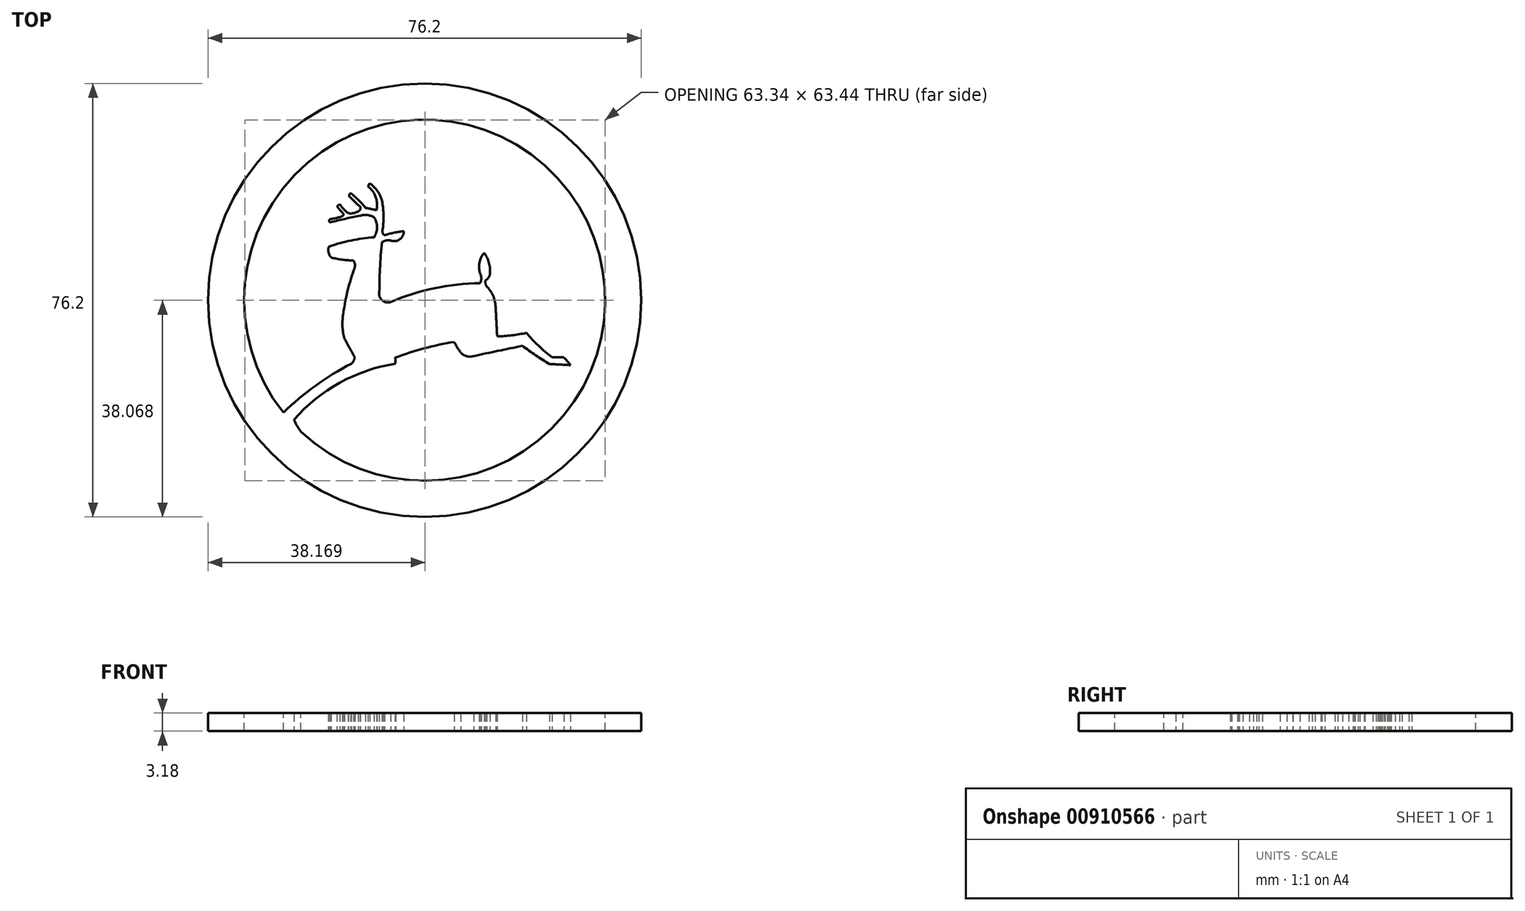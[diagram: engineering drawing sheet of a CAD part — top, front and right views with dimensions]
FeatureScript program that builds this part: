
annotation { "Feature Type Name" : "Feature", "Feature Type Description" : "" }
export const myFeature = defineFeature(function(context is Context, id is Id, definition is map)
    precondition{}
    {
        {
            var Q0;
            Q0=qCreatedBy(makeId("Top.planeOp"),FACE);
            var sketch = newSketch(context, id + "F0", { "sketchPlane" : qUnion([Q0])});
            skArc(sketch, "E0", {"start": v(40.39, 34.09) * mm, "mid": v(30.63, 30.74) * mm, "end": v(22.62, 24.25) * mm});
            skArc(sketch, "E1", {"start": v(50.78, 37.92) * mm, "mid": v(45.51, 36.8) * mm, "end": v(40.39, 35.14) * mm});
            skArc(sketch, "E2", {"start": v(40.39, 34.09) * mm, "mid": v(40.48, 34.61) * mm, "end": v(40.39, 35.14) * mm});
            skArc(sketch, "E3", {"start": v(50.78, 37.92) * mm, "mid": v(51.3, 36.98) * mm, "end": v(51.92, 36.1) * mm});
            skArc(sketch, "E4", {"start": v(51.92, 36.1) * mm, "mid": v(52.98, 35.4) * mm, "end": v(54.24, 35.43) * mm});
            skArc(sketch, "E5", {"start": v(62.79, 37.23) * mm, "mid": v(58.51, 36.35) * mm, "end": v(54.24, 35.43) * mm});
            skArc(sketch, "E6", {"start": v(62.79, 37.23) * mm, "mid": v(65.13, 35.57) * mm, "end": v(67.57, 34.04) * mm});
            skArc(sketch, "E7", {"start": v(71.27, 33.84) * mm, "mid": v(69.42, 33.94) * mm, "end": v(67.57, 34.04) * mm});
            skArc(sketch, "E8", {"start": v(71.27, 33.84) * mm, "mid": v(70.7, 34.53) * mm, "end": v(70.1, 35.2) * mm});
            skArc(sketch, "E9", {"start": v(63.47, 39.51) * mm, "mid": v(65.64, 37.24) * mm, "end": v(68.03, 35.2) * mm});
            skArc(sketch, "E10", {"start": v(58.35, 38.9) * mm, "mid": v(60.92, 39.08) * mm, "end": v(63.47, 39.51) * mm});
            skArc(sketch, "E11", {"start": v(58.35, 38.9) * mm, "mid": v(58.22, 41.35) * mm, "end": v(58.07, 43.8) * mm});
            skArc(sketch, "E12", {"start": v(58.07, 43.8) * mm, "mid": v(57.7, 45.9) * mm, "end": v(56.5, 47.67) * mm});
            skArc(sketch, "E13", {"start": v(57.07, 49.79) * mm, "mid": v(56.92, 51.78) * mm, "end": v(56.07, 53.6) * mm});
            skArc(sketch, "E14", {"start": v(56.07, 53.6) * mm, "mid": v(55.23, 51.88) * mm, "end": v(55.34, 49.97) * mm});
            skArc(sketch, "E15", {"start": v(55.34, 48.24) * mm, "mid": v(55.55, 49.1) * mm, "end": v(55.34, 49.97) * mm});
            skArc(sketch, "E16", {"start": v(56.3, 48.76) * mm, "mid": v(56.79, 49.2) * mm, "end": v(57.07, 49.79) * mm});
            skArc(sketch, "E17", {"start": v(56.3, 48.76) * mm, "mid": v(56.3, 48.2) * mm, "end": v(56.5, 47.67) * mm});
            skArc(sketch, "E18", {"start": v(55.34, 48.24) * mm, "mid": v(47.3, 47.38) * mm, "end": v(39.62, 44.91) * mm});
            skArc(sketch, "E19", {"start": v(37.6, 46.1) * mm, "mid": v(38.36, 45.07) * mm, "end": v(39.62, 44.91) * mm});
            skArc(sketch, "E20", {"start": v(38.07, 55.46) * mm, "mid": v(37.73, 50.79) * mm, "end": v(37.6, 46.1) * mm});
            skArc(sketch, "E21", {"start": v(39.62, 55.76) * mm, "mid": v(38.81, 55.75) * mm, "end": v(38.07, 55.46) * mm});
            skArc(sketch, "E22", {"start": v(39.62, 55.76) * mm, "mid": v(41.2, 55.96) * mm, "end": v(41.92, 57.4) * mm});
            skArc(sketch, "E23", {"start": v(41.92, 57.4) * mm, "mid": v(40.22, 57.13) * mm, "end": v(38.57, 56.67) * mm});
            skArc(sketch, "E24", {"start": v(36.68, 56.33) * mm, "mid": v(37.22, 58.07) * mm, "end": v(36.7, 59.81) * mm});
            skArc(sketch, "E25", {"start": v(36.7, 59.81) * mm, "mid": v(35.48, 60.24) * mm, "end": v(34.2, 60.09) * mm});
            skArc(sketch, "E26", {"start": v(34.2, 60.09) * mm, "mid": v(31.6, 59.57) * mm, "end": v(29.02, 58.95) * mm});
            skArc(sketch, "E27", {"start": v(29.02, 59.52) * mm, "mid": v(28.8, 59.23) * mm, "end": v(29.02, 58.95) * mm});
            skArc(sketch, "E28", {"start": v(29.02, 59.52) * mm, "mid": v(30.14, 59.73) * mm, "end": v(31.23, 60.09) * mm});
            skArc(sketch, "E29", {"start": v(31.23, 60.09) * mm, "mid": v(31.3, 60.34) * mm, "end": v(31.23, 60.59) * mm});
            skArc(sketch, "E30", {"start": v(30.18, 61.75) * mm, "mid": v(30.68, 61.15) * mm, "end": v(31.23, 60.59) * mm});
            skArc(sketch, "E31", {"start": v(37.13, 61.1) * mm, "mid": v(36.16, 61.3) * mm, "end": v(35.2, 61.5) * mm});
            skArc(sketch, "E32", {"start": v(33.87, 60.9) * mm, "mid": v(34.3, 61.41) * mm, "end": v(33.9, 61.96) * mm});
            skArc(sketch, "E33", {"start": v(32.12, 60.59) * mm, "mid": v(33.03, 60.55) * mm, "end": v(33.87, 60.9) * mm});
            skArc(sketch, "E34", {"start": v(38.18, 62.18) * mm, "mid": v(37.44, 64.22) * mm, "end": v(35.95, 65.81) * mm});
            skArc(sketch, "E35", {"start": v(37.11, 62.9) * mm, "mid": v(36.6, 64.22) * mm, "end": v(35.63, 65.25) * mm});
            skArc(sketch, "E36", {"start": v(37.13, 61.1) * mm, "mid": v(37.23, 62) * mm, "end": v(37.11, 62.9) * mm});
            skArc(sketch, "E37", {"start": v(35.2, 61.5) * mm, "mid": v(33.95, 62.87) * mm, "end": v(32.57, 64.1) * mm});
            skArc(sketch, "E38", {"start": v(33.9, 61.96) * mm, "mid": v(33.07, 62.81) * mm, "end": v(32.2, 63.63) * mm});
            skArc(sketch, "E39", {"start": v(38.18, 57.56) * mm, "mid": v(38.36, 59.87) * mm, "end": v(38.18, 62.18) * mm});
            skArc(sketch, "E40", {"start": v(38.18, 57.56) * mm, "mid": v(38.22, 57.05) * mm, "end": v(38.57, 56.67) * mm});
            skArc(sketch, "E41", {"start": v(30.64, 62.18) * mm, "mid": v(31.3, 61.32) * mm, "end": v(32.12, 60.59) * mm});
            skLineSegment(sketch, "E42", {"start": v(35.95, 65.81) * mm, "end": v(35.63, 65.25) * mm});
            skLineSegment(sketch, "E43", {"start": v(32.57, 64.1) * mm, "end": v(32.2, 63.63) * mm});
            skLineSegment(sketch, "E44", {"start": v(30.64, 62.18) * mm, "end": v(30.18, 61.75) * mm});
            skArc(sketch, "E45", {"start": v(36.68, 56.33) * mm, "mid": v(32.65, 55.75) * mm, "end": v(28.73, 54.69) * mm});
            skArc(sketch, "E46", {"start": v(28.73, 54.69) * mm, "mid": v(28.69, 53.68) * mm, "end": v(29.14, 52.77) * mm});
            skArc(sketch, "E47", {"start": v(29.14, 52.77) * mm, "mid": v(31.11, 52.39) * mm, "end": v(33.1, 52.25) * mm});
            skArc(sketch, "E48", {"start": v(33.1, 50.5) * mm, "mid": v(33.32, 51.37) * mm, "end": v(33.1, 52.25) * mm});
            skArc(sketch, "E49", {"start": v(33.1, 50.5) * mm, "mid": v(31.96, 46.61) * mm, "end": v(31.24, 42.63) * mm});
            skArc(sketch, "E50", {"start": v(31.24, 42.63) * mm, "mid": v(31.14, 40.54) * mm, "end": v(31.51, 38.49) * mm});
            skArc(sketch, "E51", {"start": v(31.51, 38.49) * mm, "mid": v(32.37, 36.88) * mm, "end": v(33.27, 35.3) * mm});
            skArc(sketch, "E52", {"start": v(32.68, 34.11) * mm, "mid": v(33.11, 34.63) * mm, "end": v(33.27, 35.3) * mm});
            skArc(sketch, "E53", {"start": v(32.68, 34.11) * mm, "mid": v(25.94, 29.89) * mm, "end": v(19.92, 24.7) * mm});
            skLineSegment(sketch, "E54", {"start": v(19.92, 24.7) * mm, "end": v(22.62, 24.25) * mm});
            skLineSegment(sketch, "E55", {"start": v(70.1, 35.2) * mm, "end": v(68.03, 35.2) * mm});
            skLineSegment(sketch, "E56", {"start": v(29.13, 16.25) * mm, "end": v(29.13, 22.07) * mm});
            skLineSegment(sketch, "E57", {"start": v(29.13, 22.07) * mm, "end": v(30.21, 22.07) * mm});
            skLineSegment(sketch, "E58", {"start": v(30.21, 22.07) * mm, "end": v(30.21, 19.61) * mm});
            skLineSegment(sketch, "E59", {"start": v(30.21, 19.61) * mm, "end": v(32.67, 19.61) * mm});
            skLineSegment(sketch, "E60", {"start": v(32.67, 19.61) * mm, "end": v(32.67, 22.04) * mm});
            skLineSegment(sketch, "E61", {"start": v(32.67, 22.04) * mm, "end": v(33.65, 22.04) * mm});
            skLineSegment(sketch, "E62", {"start": v(33.65, 22.04) * mm, "end": v(33.65, 16.25) * mm});
            skLineSegment(sketch, "E63", {"start": v(33.65, 16.25) * mm, "end": v(32.67, 16.25) * mm});
            skLineSegment(sketch, "E64", {"start": v(32.67, 16.25) * mm, "end": v(32.67, 18.82) * mm});
            skLineSegment(sketch, "E65", {"start": v(32.67, 18.82) * mm, "end": v(30.21, 18.82) * mm});
            skLineSegment(sketch, "E66", {"start": v(30.21, 18.82) * mm, "end": v(30.21, 16.25) * mm});
            skLineSegment(sketch, "E67", {"start": v(30.21, 16.25) * mm, "end": v(29.13, 16.25) * mm});
            skLineSegment(sketch, "E68", {"start": v(35.57, 16.25) * mm, "end": v(35.57, 22.04) * mm});
            skLineSegment(sketch, "E69", {"start": v(35.57, 22.04) * mm, "end": v(36.54, 22.04) * mm});
            skLineSegment(sketch, "E70", {"start": v(36.54, 22.04) * mm, "end": v(39.11, 18.31) * mm});
            skLineSegment(sketch, "E71", {"start": v(39.11, 18.31) * mm, "end": v(39.11, 22.04) * mm});
            skLineSegment(sketch, "E72", {"start": v(39.11, 22.04) * mm, "end": v(40.27, 22.04) * mm});
            skLineSegment(sketch, "E73", {"start": v(40.27, 22.04) * mm, "end": v(40.27, 16.25) * mm});
            skLineSegment(sketch, "E74", {"start": v(40.27, 16.25) * mm, "end": v(39.11, 16.25) * mm});
            skLineSegment(sketch, "E75", {"start": v(39.11, 16.25) * mm, "end": v(36.54, 19.98) * mm});
            skLineSegment(sketch, "E76", {"start": v(36.54, 19.98) * mm, "end": v(36.54, 16.25) * mm});
            skLineSegment(sketch, "E77", {"start": v(36.54, 16.25) * mm, "end": v(35.57, 16.25) * mm});
            skLineSegment(sketch, "E78", {"start": v(20.88, 22.04) * mm, "end": v(20.88, 17.08) * mm});
            skLineSegment(sketch, "E79", {"start": v(20.88, 22.04) * mm, "end": v(19.72, 22.04) * mm});
            skLineSegment(sketch, "E80", {"start": v(19.72, 22.04) * mm, "end": v(19.72, 17.48) * mm});
            skLineSegment(sketch, "E81", {"start": v(18.28, 18.1) * mm, "end": v(17.26, 18.1) * mm});
            skLineSegment(sketch, "E82", {"start": v(44.1, 16.25) * mm, "end": v(44.1, 22.04) * mm});
            skLineSegment(sketch, "E83", {"start": v(44.1, 22.04) * mm, "end": v(44.82, 22.04) * mm});
            skLineSegment(sketch, "E84", {"start": v(44.82, 22.04) * mm, "end": v(44.82, 16.25) * mm});
            skLineSegment(sketch, "E85", {"start": v(44.82, 16.25) * mm, "end": v(44.1, 16.25) * mm});
            skLineSegment(sketch, "E86", {"start": v(45.22, 16.25) * mm, "end": v(45.22, 16.82) * mm});
            skLineSegment(sketch, "E87", {"start": v(45.22, 16.82) * mm, "end": v(46.72, 16.82) * mm});
            skLineSegment(sketch, "E88", {"start": v(45.22, 16.25) * mm, "end": v(46.72, 16.25) * mm});
            skLineSegment(sketch, "E89", {"start": v(45.22, 22.04) * mm, "end": v(45.22, 21.44) * mm});
            skLineSegment(sketch, "E90", {"start": v(45.22, 21.44) * mm, "end": v(46.72, 21.44) * mm});
            skLineSegment(sketch, "E91", {"start": v(45.22, 22.04) * mm, "end": v(46.72, 22.04) * mm});
            skLineSegment(sketch, "E92", {"start": v(50.5, 16.25) * mm, "end": v(50.5, 22.04) * mm});
            skLineSegment(sketch, "E93", {"start": v(50.5, 22.04) * mm, "end": v(54.34, 22.04) * mm});
            skLineSegment(sketch, "E94", {"start": v(54.34, 22.04) * mm, "end": v(54.34, 21.44) * mm});
            skLineSegment(sketch, "E95", {"start": v(54.34, 21.44) * mm, "end": v(51.26, 21.44) * mm});
            skLineSegment(sketch, "E96", {"start": v(51.26, 21.44) * mm, "end": v(51.26, 19.54) * mm});
            skLineSegment(sketch, "E97", {"start": v(51.26, 19.54) * mm, "end": v(54.05, 19.54) * mm});
            skLineSegment(sketch, "E98", {"start": v(54.05, 19.54) * mm, "end": v(54.05, 18.92) * mm});
            skLineSegment(sketch, "E99", {"start": v(54.05, 18.92) * mm, "end": v(51.26, 18.92) * mm});
            skLineSegment(sketch, "E100", {"start": v(51.26, 18.92) * mm, "end": v(51.26, 16.82) * mm});
            skLineSegment(sketch, "E101", {"start": v(51.26, 16.82) * mm, "end": v(54.34, 16.82) * mm});
            skLineSegment(sketch, "E102", {"start": v(54.34, 16.82) * mm, "end": v(54.34, 16.25) * mm});
            skLineSegment(sketch, "E103", {"start": v(54.34, 16.25) * mm, "end": v(50.5, 16.25) * mm});
            skLineSegment(sketch, "E104", {"start": v(62, 16.25) * mm, "end": v(62, 22.04) * mm});
            skLineSegment(sketch, "E105", {"start": v(62, 22.04) * mm, "end": v(64.54, 22.04) * mm});
            skLineSegment(sketch, "E106", {"start": v(62, 16.25) * mm, "end": v(62.76, 16.25) * mm});
            skLineSegment(sketch, "E107", {"start": v(62.76, 16.25) * mm, "end": v(62.76, 21.44) * mm});
            skLineSegment(sketch, "E108", {"start": v(62.76, 21.44) * mm, "end": v(64.54, 21.44) * mm});
            skLineSegment(sketch, "E109", {"start": v(63.29, 18.62) * mm, "end": v(63.29, 19.38) * mm});
            skLineSegment(sketch, "E110", {"start": v(63.29, 19.38) * mm, "end": v(64.4, 19.38) * mm});
            skLineSegment(sketch, "E111", {"start": v(63.29, 18.62) * mm, "end": v(64.4, 18.62) * mm});
            skLineSegment(sketch, "E112", {"start": v(66.27, 16.25) * mm, "end": v(65.48, 16.25) * mm});
            skLineSegment(sketch, "E113", {"start": v(65.48, 16.25) * mm, "end": v(65.2, 16.25) * mm});
            skLineSegment(sketch, "E114", {"start": v(65.2, 16.25) * mm, "end": v(65.2, 17.06) * mm});
            skLineSegment(sketch, "E115", {"start": v(66.27, 16.25) * mm, "end": v(66.27, 17.46) * mm});
            skArc(sketch, "E116", {"start": v(65.2, 17.06) * mm, "mid": v(65, 17.93) * mm, "end": v(64.4, 18.62) * mm});
            skArc(sketch, "E117", {"start": v(66.27, 17.46) * mm, "mid": v(66.02, 18.34) * mm, "end": v(65.35, 18.96) * mm});
            skArc(sketch, "E118", {"start": v(64.4, 19.38) * mm, "mid": v(65.29, 20.36) * mm, "end": v(64.54, 21.44) * mm});
            skArc(sketch, "E119", {"start": v(65.35, 18.96) * mm, "mid": v(66.13, 20.8) * mm, "end": v(64.54, 22.04) * mm});
            skArc(sketch, "E120", {"start": v(46.72, 16.82) * mm, "mid": v(48.1, 19.13) * mm, "end": v(46.72, 21.44) * mm});
            skArc(sketch, "E121", {"start": v(46.72, 16.25) * mm, "mid": v(49.06, 19.14) * mm, "end": v(46.72, 22.04) * mm});
            skArc(sketch, "E122", {"start": v(17.26, 18.1) * mm, "mid": v(18.6, 15.92) * mm, "end": v(20.88, 17.08) * mm});
            skArc(sketch, "E123", {"start": v(18.28, 18.1) * mm, "mid": v(18.69, 17.06) * mm, "end": v(19.72, 17.48) * mm});
            skArc(sketch, "E124", {"start": v(24.69, 22.04) * mm, "mid": v(22.14, 19.05) * mm, "end": v(24.58, 15.97) * mm});
            skArc(sketch, "E125", {"start": v(25.49, 15.97) * mm, "mid": v(28.02, 18.97) * mm, "end": v(25.56, 22.04) * mm});
            skArc(sketch, "E126", {"start": v(24.69, 21.5) * mm, "mid": v(23.18, 19.2) * mm, "end": v(24.58, 16.82) * mm});
            skArc(sketch, "E127", {"start": v(25.49, 16.79) * mm, "mid": v(27.04, 19.1) * mm, "end": v(25.56, 21.44) * mm});
            skLineSegment(sketch, "E128", {"start": v(25.56, 21.44) * mm, "end": v(25.56, 22.04) * mm});
            skLineSegment(sketch, "E129", {"start": v(24.58, 16.82) * mm, "end": v(24.58, 15.97) * mm});
            skLineSegment(sketch, "E130", {"start": v(24.69, 22.04) * mm, "end": v(24.69, 21.5) * mm});
            skLineSegment(sketch, "E131", {"start": v(25.49, 15.97) * mm, "end": v(25.49, 16.79) * mm});
            skLineSegment(sketch, "E132", {"start": v(56.01, 16.25) * mm, "end": v(56.01, 22.04) * mm});
            skLineSegment(sketch, "E133", {"start": v(56.01, 22.04) * mm, "end": v(60.38, 22.04) * mm});
            skLineSegment(sketch, "E134", {"start": v(60.38, 22.04) * mm, "end": v(60.38, 21.44) * mm});
            skLineSegment(sketch, "E135", {"start": v(60.38, 21.44) * mm, "end": v(57.13, 21.44) * mm});
            skLineSegment(sketch, "E136", {"start": v(57.13, 21.44) * mm, "end": v(57.13, 19.54) * mm});
            skLineSegment(sketch, "E137", {"start": v(57.13, 19.54) * mm, "end": v(59.83, 19.54) * mm});
            skLineSegment(sketch, "E138", {"start": v(59.83, 19.54) * mm, "end": v(59.83, 18.92) * mm});
            skLineSegment(sketch, "E139", {"start": v(59.83, 18.92) * mm, "end": v(57.13, 18.92) * mm});
            skLineSegment(sketch, "E140", {"start": v(57.13, 18.92) * mm, "end": v(57.13, 16.82) * mm});
            skLineSegment(sketch, "E141", {"start": v(57.13, 16.82) * mm, "end": v(60.38, 16.82) * mm});
            skLineSegment(sketch, "E142", {"start": v(60.38, 16.82) * mm, "end": v(60.38, 16.25) * mm});
            skLineSegment(sketch, "E143", {"start": v(60.38, 16.25) * mm, "end": v(56.01, 16.25) * mm});
            skLineSegment(sketch, "E144", {"start": v(67.98, 16.25) * mm, "end": v(67.98, 22.04) * mm});
            skLineSegment(sketch, "E145", {"start": v(67.98, 22.04) * mm, "end": v(72.15, 22.04) * mm});
            skLineSegment(sketch, "E146", {"start": v(72.15, 22.04) * mm, "end": v(72.15, 21.44) * mm});
            skLineSegment(sketch, "E147", {"start": v(72.15, 21.44) * mm, "end": v(68.99, 21.44) * mm});
            skLineSegment(sketch, "E148", {"start": v(68.99, 21.44) * mm, "end": v(68.99, 19.54) * mm});
            skLineSegment(sketch, "E149", {"start": v(68.99, 19.54) * mm, "end": v(71.8, 19.54) * mm});
            skLineSegment(sketch, "E150", {"start": v(71.8, 19.54) * mm, "end": v(71.8, 18.92) * mm});
            skLineSegment(sketch, "E151", {"start": v(68.99, 18.92) * mm, "end": v(68.99, 16.82) * mm});
            skLineSegment(sketch, "E152", {"start": v(68.99, 16.82) * mm, "end": v(72.15, 16.82) * mm});
            skLineSegment(sketch, "E153", {"start": v(67.98, 16.25) * mm, "end": v(72.15, 16.25) * mm});
            skLineSegment(sketch, "E154", {"start": v(72.15, 16.25) * mm, "end": v(72.15, 16.82) * mm});
            skLineSegment(sketch, "E155", {"start": v(71.8, 18.92) * mm, "end": v(68.99, 18.92) * mm});
            skPoint(sketch, "E156.orphan", {"position": v(71.8, 16.82) * mm});
            skLineSegment(sketch, "E157.bottom", {"start": v(5.26, 72.42) * mm, "end": v(87.73, 72.42) * mm});
            skLineSegment(sketch, "E157.top", {"start": v(5.26, 9.48) * mm, "end": v(87.73, 9.48) * mm});
            skLineSegment(sketch, "E157.left", {"start": v(5.26, 72.42) * mm, "end": v(5.26, 9.48) * mm});
            skLineSegment(sketch, "E157.right", {"start": v(87.73, 72.42) * mm, "end": v(87.73, 9.48) * mm});
            skPoint(sketch, "E158.endSnap0", {"position": v(60.92, 39.08) * mm});
            skSolve(sketch);
        }
        {
            var Q0;
            Q0=makeQuery(id+"F0.imprint","IMPRINT",FACE,{"disambiguationData":[TD([[makeQuery(id+"F0.imprint","IMPRINT",EDGE,{"derivedFrom":sQuery(id+"F0.wireOp",EDGE,"E0")}),-1.0]])]});
            extrude(context, id + "F1", {"entities" : qUnion([Q0]), "depth" : 3.17 * mm, "offsetDistance" : 25.4 * mm});
        }
        {
            var Q0;
            Q0=makeQuery(id+"F1.opExtrude","CAP_FACE",FACE,{"disambiguationData":[OSD([sQuery(id+"F0.wireOp",EDGE,"E0"),sQuery(id+"F0.wireOp",EDGE,"E1"),sQuery(id+"F0.wireOp",EDGE,"E2"),sQuery(id+"F0.wireOp",EDGE,"E3"),sQuery(id+"F0.wireOp",EDGE,"E4"),sQuery(id+"F0.wireOp",EDGE,"E5"),sQuery(id+"F0.wireOp",EDGE,"E6"),sQuery(id+"F0.wireOp",EDGE,"E7"),sQuery(id+"F0.wireOp",EDGE,"E8"),sQuery(id+"F0.wireOp",EDGE,"E9"),sQuery(id+"F0.wireOp",EDGE,"E10"),sQuery(id+"F0.wireOp",EDGE,"E11"),sQuery(id+"F0.wireOp",EDGE,"E12"),sQuery(id+"F0.wireOp",EDGE,"E13"),sQuery(id+"F0.wireOp",EDGE,"E14"),sQuery(id+"F0.wireOp",EDGE,"E15"),sQuery(id+"F0.wireOp",EDGE,"E16"),sQuery(id+"F0.wireOp",EDGE,"E17"),sQuery(id+"F0.wireOp",EDGE,"E18"),sQuery(id+"F0.wireOp",EDGE,"E19"),sQuery(id+"F0.wireOp",EDGE,"E20"),sQuery(id+"F0.wireOp",EDGE,"E21"),sQuery(id+"F0.wireOp",EDGE,"E22"),sQuery(id+"F0.wireOp",EDGE,"E23"),sQuery(id+"F0.wireOp",EDGE,"E24"),sQuery(id+"F0.wireOp",EDGE,"E25"),sQuery(id+"F0.wireOp",EDGE,"E26"),sQuery(id+"F0.wireOp",EDGE,"E27"),sQuery(id+"F0.wireOp",EDGE,"E28"),sQuery(id+"F0.wireOp",EDGE,"E29"),sQuery(id+"F0.wireOp",EDGE,"E30"),sQuery(id+"F0.wireOp",EDGE,"E31"),sQuery(id+"F0.wireOp",EDGE,"E32"),sQuery(id+"F0.wireOp",EDGE,"E33"),sQuery(id+"F0.wireOp",EDGE,"E34"),sQuery(id+"F0.wireOp",EDGE,"E35"),sQuery(id+"F0.wireOp",EDGE,"E36"),sQuery(id+"F0.wireOp",EDGE,"E37"),sQuery(id+"F0.wireOp",EDGE,"E38"),sQuery(id+"F0.wireOp",EDGE,"E39"),sQuery(id+"F0.wireOp",EDGE,"E40"),sQuery(id+"F0.wireOp",EDGE,"E41"),sQuery(id+"F0.wireOp",EDGE,"E42"),sQuery(id+"F0.wireOp",EDGE,"E43"),sQuery(id+"F0.wireOp",EDGE,"E44"),sQuery(id+"F0.wireOp",EDGE,"E45"),sQuery(id+"F0.wireOp",EDGE,"E46"),sQuery(id+"F0.wireOp",EDGE,"E47"),sQuery(id+"F0.wireOp",EDGE,"E48"),sQuery(id+"F0.wireOp",EDGE,"E49"),sQuery(id+"F0.wireOp",EDGE,"E50"),sQuery(id+"F0.wireOp",EDGE,"E51"),sQuery(id+"F0.wireOp",EDGE,"E52"),sQuery(id+"F0.wireOp",EDGE,"E53"),sQuery(id+"F0.wireOp",EDGE,"E54"),sQuery(id+"F0.wireOp",EDGE,"E55")])],"isStart":false});
            var sketch = newSketch(context, id + "F2", { "sketchPlane" : qUnion([Q0])});
            skLineSegment(sketch, "E159", {"start": v(22.62, 24.25) * mm, "end": v(22.62, 65.25) * mm});
            skLineSegment(sketch, "E160", {"start": v(19.92, 24.7) * mm, "end": v(71.27, 24.7) * mm});
            skLineSegment(sketch, "E161", {"start": v(45.6, 24.7) * mm, "end": v(45.6, 65.81) * mm});
            skCircle(sketch, "E162", {"center": v(45.6, 45.26) * mm, "radius": 38.1 * mm});
            skCircle(sketch, "E163.0", {"center": v(45.6, 45.26) * mm, "radius": 31.75 * mm});
            skArc(sketch, "E164", {"start": v(22.62, 24.25) * mm, "mid": v(23.15, 23.17) * mm, "end": v(23.8, 22.16) * mm});
            skSolve(sketch);
        }
        {
            var Q0;
            Q0=makeQuery(id+"F2.imprint","IMPRINT",FACE,{"disambiguationData":[TD([[makeQuery(id+"F2.imprint","IMPRINT",EDGE,{"derivedFrom":sQuery(id+"F2.wireOp",EDGE,"E162")}),1.0]])]});
            var Q1;
            {var subQ0=sQuery(id+"F2.wireOp",EDGE,"E164");Q1=makeQuery(id+"F2.imprint","IMPRINT",FACE,{"disambiguationData":[TD([[makeQuery(id+"F2.imprint","IMPRINT",EDGE,{"derivedFrom":subQ0}),-1.0]])]});}
            extrude(context, id + "F3", {"entities" : qUnion([Q0, Q1]), "operationType" : NewBodyOperationType.ADD, "oppositeDirection" : true, "depth" : 3.17 * mm, "offsetDistance" : 25.4 * mm});
        }
    });
